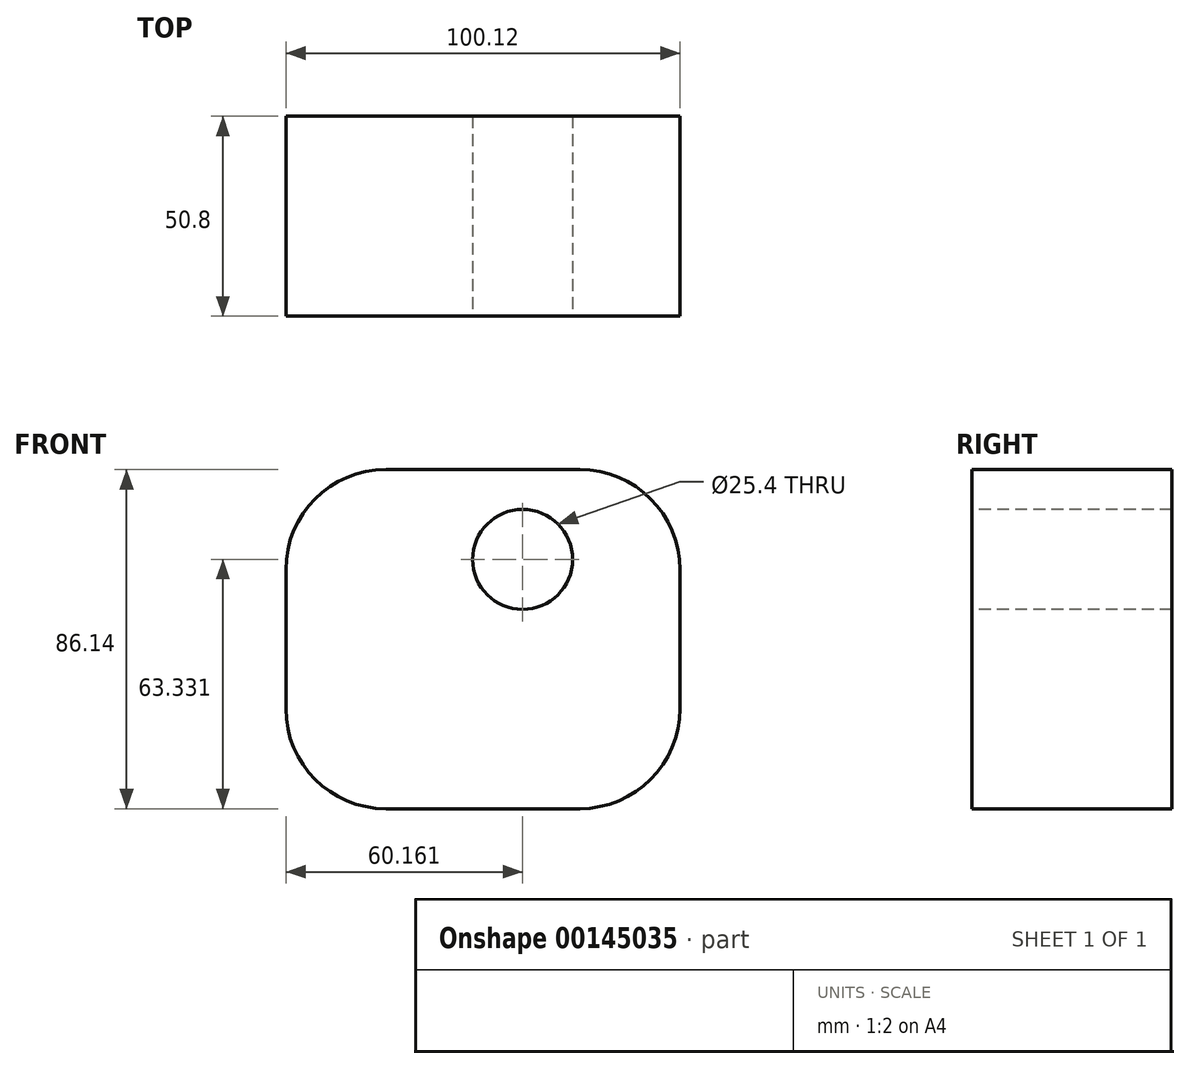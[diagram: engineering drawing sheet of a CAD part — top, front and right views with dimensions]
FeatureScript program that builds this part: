
annotation { "Feature Type Name" : "Feature", "Feature Type Description" : "" }
export const myFeature = defineFeature(function(context is Context, id is Id, definition is map)
    precondition{}
    {
        {
            var Q0;
            Q0=qCreatedBy(makeId("Front.planeOp"),FACE);
            var sketch = newSketch(context, id + "F0", { "sketchPlane" : qUnion([Q0])});
            skLineSegment(sketch, "E0.bottom", {"start": v(-48.5, 52.34) * mm, "end": v(51.63, 52.34) * mm});
            skLineSegment(sketch, "E0.top", {"start": v(-48.5, -33.8) * mm, "end": v(51.63, -33.8) * mm});
            skLineSegment(sketch, "E0.left", {"start": v(-48.5, 52.34) * mm, "end": v(-48.5, -33.8) * mm});
            skLineSegment(sketch, "E0.right", {"start": v(51.63, 52.34) * mm, "end": v(51.63, -33.8) * mm});
            skSolve(sketch);
        }
        {
            var Q0;
            Q0 = qSketchRegion(id + "F0", true);
            extrude(context, id + "F1", {"entities" : qUnion([Q0]), "depth" : 50.8 * mm});
        }
        {
            var Q0;
            Q0=makeQuery(id+"F1.opExtrude","SWEPT_EDGE",EDGE,{"disambiguationData":[OSD([sQuery(id+"F0.wireOp",EDGE,"E0.bottom"),sQuery(id+"F0.wireOp",EDGE,"E0.right")])]});
            var Q1;
            Q1=makeQuery(id+"F1.opExtrude","SWEPT_EDGE",EDGE,{"disambiguationData":[OSD([sQuery(id+"F0.wireOp",EDGE,"E0.bottom"),sQuery(id+"F0.wireOp",EDGE,"E0.left")])]});
            var Q2;
            Q2=makeQuery(id+"F1.opExtrude","SWEPT_EDGE",EDGE,{"disambiguationData":[OSD([sQuery(id+"F0.wireOp",EDGE,"E0.top"),sQuery(id+"F0.wireOp",EDGE,"E0.left")])]});
            var Q3;
            Q3=makeQuery(id+"F1.opExtrude","SWEPT_EDGE",EDGE,{"disambiguationData":[OSD([sQuery(id+"F0.wireOp",EDGE,"E0.top"),sQuery(id+"F0.wireOp",EDGE,"E0.right")])]});
            fillet(context, id + "F2", {"entities" : qUnion([Q0, Q1, Q2, Q3]), "radius" : 25.4 * mm, "tangentPropagation" : true, "allowEdgeOverflow" : false});
        }
        {
            var Q0;
            Q0=makeQuery(id+"F1.opExtrude","CAP_FACE",FACE,{"disambiguationData":[OSD([sQuery(id+"F0.wireOp",EDGE,"E0.bottom"),sQuery(id+"F0.wireOp",EDGE,"E0.top"),sQuery(id+"F0.wireOp",EDGE,"E0.left"),sQuery(id+"F0.wireOp",EDGE,"E0.right")])],"isStart":false});
            var sketch = newSketch(context, id + "F3", { "sketchPlane" : qUnion([Q0])});
            skCircle(sketch, "E1", {"center": v(11.67, 29.53) * mm, "radius": 15.18 * mm});
            skSolve(sketch);
        }
        {
            var Q0;
            Q0=sQuery(id+"F3.wireOp",VERTEX,"E1.center");
            var Q1;
            Q1=makeQuery(id+"F1.opExtrude","SWEPT_BODY",BODY,{"disambiguationData":[OSD([sQuery(id+"F0.wireOp",EDGE,"E0.bottom"),sQuery(id+"F0.wireOp",EDGE,"E0.top"),sQuery(id+"F0.wireOp",EDGE,"E0.left"),sQuery(id+"F0.wireOp",EDGE,"E0.right")])]});
            hole(context, id + "F4", {"style" : HoleStyle.SIMPLE, "endStyle" : HoleEndStyle.THROUGH, "holeDiameter" : 25.4 * mm, "locations" : qUnion([Q0]), "scope" : qUnion([Q1]), "isTappedThrough" : true});
        }
    });
